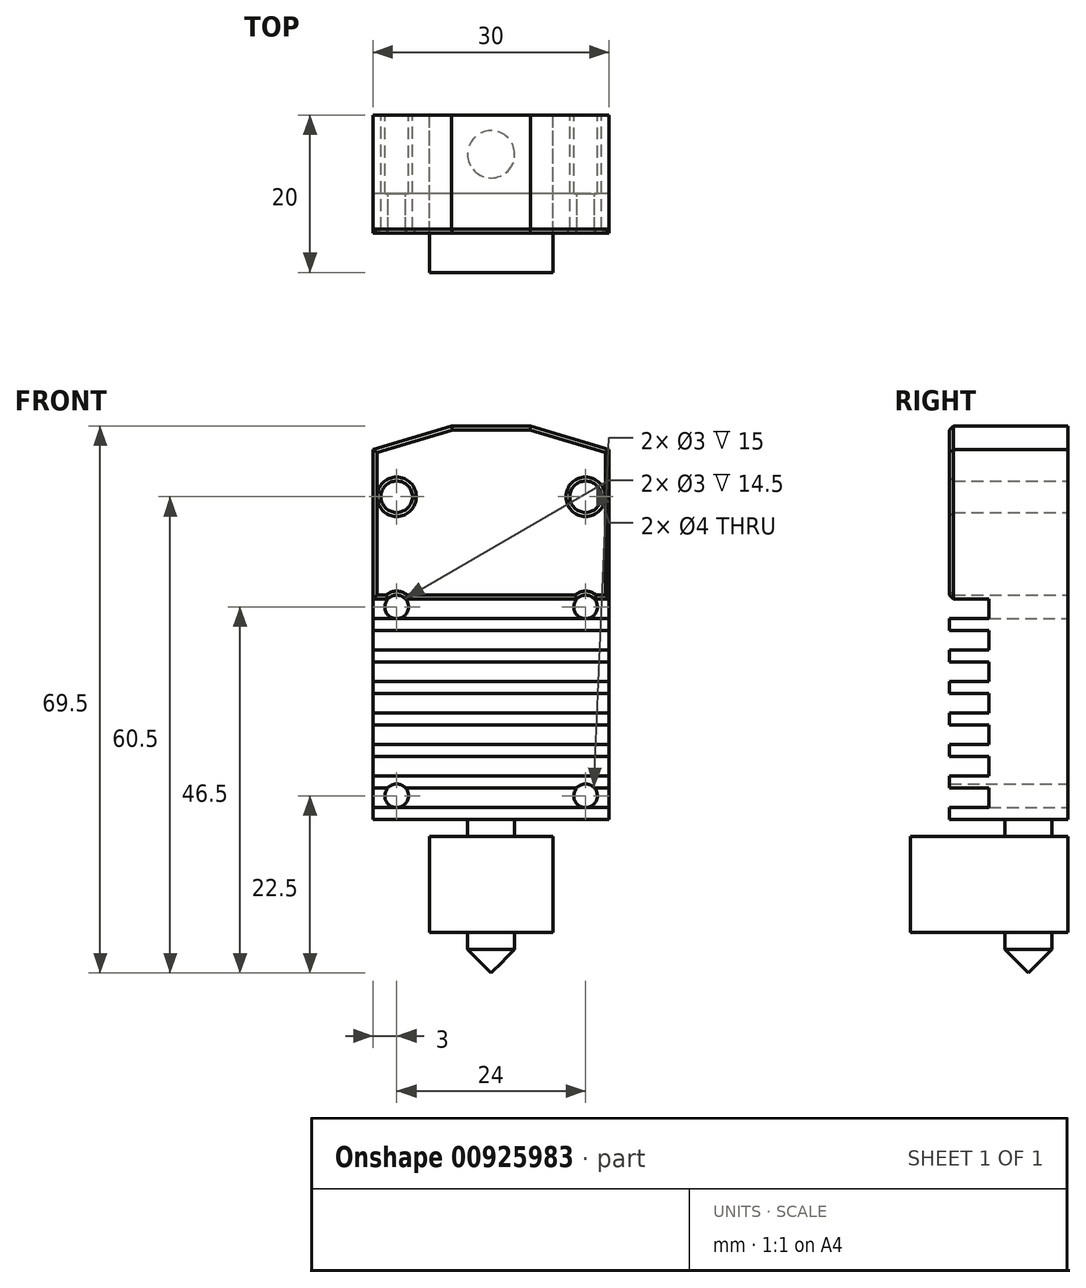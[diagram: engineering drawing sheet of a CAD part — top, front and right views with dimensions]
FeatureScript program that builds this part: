
annotation { "Feature Type Name" : "Feature", "Feature Type Description" : "" }
export const myFeature = defineFeature(function(context is Context, id is Id, definition is map)
    precondition{}
    {
        {
            var Q0;
            Q0=qCreatedBy(makeId("Front.planeOp"),FACE);
            var sketch = newSketch(context, id + "F0", { "sketchPlane" : qUnion([Q0])});
            skLineSegment(sketch, "E0", {"start": v(0, 0) * mm, "end": v(-15, 0) * mm});
            skLineSegment(sketch, "E1", {"start": v(-15, 0) * mm, "end": v(-15, -50) * mm});
            skLineSegment(sketch, "E2", {"start": v(-15, -50) * mm, "end": v(0, -50) * mm});
            skLineSegment(sketch, "E3", {"start": v(0, 0) * mm, "end": v(0, -50) * mm, "construction": true});
            skLineSegment(sketch, "E4.MirrorCS", {"start": v(0, 0) * mm, "end": v(15, 0) * mm});
            skLineSegment(sketch, "E5.MirrorCS", {"start": v(15, 0) * mm, "end": v(15, -50) * mm});
            skLineSegment(sketch, "E6.MirrorCS", {"start": v(15, -50) * mm, "end": v(0, -50) * mm});
            skCircle(sketch, "E7", {"center": v(-12, -47) * mm, "radius": 1.5 * mm});
            skCircle(sketch, "E8", {"center": v(-12, -23) * mm, "radius": 1.5 * mm});
            skCircle(sketch, "E9", {"center": v(-12, -9) * mm, "radius": 2 * mm});
            skCircle(sketch, "E10.MirrorC", {"center": v(12, -9) * mm, "radius": 2 * mm});
            skCircle(sketch, "E11.MirrorC", {"center": v(12, -23) * mm, "radius": 1.5 * mm});
            skCircle(sketch, "E12.MirrorC", {"center": v(12, -47) * mm, "radius": 1.5 * mm});
            skSolve(sketch);
        }
        {
            var Q0;
            Q0=makeQuery(id+"F0.imprint","IMPRINT",FACE,{"disambiguationData":[TD([[makeQuery(id+"F0.imprint","IMPRINT",EDGE,{"derivedFrom":sQuery(id+"F0.wireOp",EDGE,"E0")}),1.0]])]});
            extrude(context, id + "F1", {"entities" : qUnion([Q0]), "depth" : 15 * mm, "offsetDistance" : 25 * mm});
        }
        {
            var Q0;
            Q0=makeQuery(id+"F1.opExtrude","SWEPT_FACE",FACE,{"disambiguationData":[OSD([sQuery(id+"F0.wireOp",EDGE,"E1")])]});
            var sketch = newSketch(context, id + "F2", { "sketchPlane" : qUnion([Q0])});
            skLineSegment(sketch, "E13.bottom", {"start": v(15, -48.5) * mm, "end": v(10, -48.5) * mm});
            skLineSegment(sketch, "E13.top", {"start": v(15, -46) * mm, "end": v(10, -46) * mm});
            skLineSegment(sketch, "E13.left", {"start": v(15, -48.5) * mm, "end": v(15, -46) * mm});
            skLineSegment(sketch, "E13.right", {"start": v(10, -48.5) * mm, "end": v(10, -46) * mm});
            skLineSegment(sketch, "E14.0.1.0", {"start": v(15, -42) * mm, "end": v(10, -42) * mm});
            skLineSegment(sketch, "E14.0.1.1", {"start": v(15, -44.5) * mm, "end": v(10, -44.5) * mm});
            skLineSegment(sketch, "E14.0.1.2", {"start": v(10, -44.5) * mm, "end": v(10, -42) * mm});
            skLineSegment(sketch, "E14.0.1.3", {"start": v(15, -44.5) * mm, "end": v(15, -42) * mm});
            skLineSegment(sketch, "E14.0.2.0", {"start": v(15, -38) * mm, "end": v(10, -38) * mm});
            skLineSegment(sketch, "E14.0.2.1", {"start": v(15, -40.5) * mm, "end": v(10, -40.5) * mm});
            skLineSegment(sketch, "E14.0.2.2", {"start": v(10, -40.5) * mm, "end": v(10, -38) * mm});
            skLineSegment(sketch, "E14.0.2.3", {"start": v(15, -40.5) * mm, "end": v(15, -38) * mm});
            skLineSegment(sketch, "E14.0.3.0", {"start": v(15, -34) * mm, "end": v(10, -34) * mm});
            skLineSegment(sketch, "E14.0.3.1", {"start": v(15, -36.5) * mm, "end": v(10, -36.5) * mm});
            skLineSegment(sketch, "E14.0.3.2", {"start": v(10, -36.5) * mm, "end": v(10, -34) * mm});
            skLineSegment(sketch, "E14.0.3.3", {"start": v(15, -36.5) * mm, "end": v(15, -34) * mm});
            skLineSegment(sketch, "E14.0.4.0", {"start": v(15, -30) * mm, "end": v(10, -30) * mm});
            skLineSegment(sketch, "E14.0.4.1", {"start": v(15, -32.5) * mm, "end": v(10, -32.5) * mm});
            skLineSegment(sketch, "E14.0.4.2", {"start": v(10, -32.5) * mm, "end": v(10, -30) * mm});
            skLineSegment(sketch, "E14.0.4.3", {"start": v(15, -32.5) * mm, "end": v(15, -30) * mm});
            skLineSegment(sketch, "E14.0.5.0", {"start": v(15, -26) * mm, "end": v(10, -26) * mm});
            skLineSegment(sketch, "E14.0.5.1", {"start": v(15, -28.5) * mm, "end": v(10, -28.5) * mm});
            skLineSegment(sketch, "E14.0.5.2", {"start": v(10, -28.5) * mm, "end": v(10, -26) * mm});
            skLineSegment(sketch, "E14.0.5.3", {"start": v(15, -28.5) * mm, "end": v(15, -26) * mm});
            skLineSegment(sketch, "E14.0.6.0", {"start": v(15, -22) * mm, "end": v(10, -22) * mm});
            skLineSegment(sketch, "E14.0.6.1", {"start": v(15, -24.5) * mm, "end": v(10, -24.5) * mm});
            skLineSegment(sketch, "E14.0.6.2", {"start": v(10, -24.5) * mm, "end": v(10, -22) * mm});
            skLineSegment(sketch, "E14.0.6.3", {"start": v(15, -24.5) * mm, "end": v(15, -22) * mm});
            skLineSegment(sketch, "E14.direction1", {"start": v(10, -46) * mm, "end": v(40, -46) * mm, "construction": true});
            skLineSegment(sketch, "E14.direction2", {"start": v(10, -46) * mm, "end": v(10, -42) * mm, "construction": true});
            skSolve(sketch);
        }
        {
            var Q0;
            Q0 = qSketchRegion(id + "F2", true);
            extrude(context, id + "F3", {"entities" : qUnion([Q0]), "operationType" : NewBodyOperationType.REMOVE, "endBound" : BoundingType.THROUGH_ALL, "oppositeDirection" : true, "depth" : 25 * mm, "offsetDistance" : 25 * mm});
        }
        {
            var Q0;
            Q0=makeQuery(id+"F1.opExtrude","SWEPT_FACE",FACE,{"disambiguationData":[OSD([sQuery(id+"F0.wireOp",EDGE,"E2"),sQuery(id+"F0.wireOp",EDGE,"E6.MirrorCS")])]});
            var sketch = newSketch(context, id + "F4", { "sketchPlane" : qUnion([Q0])});
            skPoint(sketch, "E15.0", {"position": v(0, 10) * mm});
            skLineSegment(sketch, "E16", {"start": v(0, 0) * mm, "end": v(0, 10) * mm, "construction": true});
            skCircle(sketch, "E17", {"center": v(0, 5) * mm, "radius": 3 * mm});
            skSolve(sketch);
        }
        {
            var Q0;
            Q0=makeQuery(id+"F1.opExtrude","SWEPT_EDGE",EDGE,{"disambiguationData":[OSD([sQuery(id+"F0.wireOp",EDGE,"E0"),sQuery(id+"F0.wireOp",EDGE,"E1")])]});
            var Q1;
            Q1=makeQuery(id+"F1.opExtrude","SWEPT_EDGE",EDGE,{"disambiguationData":[OSD([sQuery(id+"F0.wireOp",EDGE,"E4.MirrorCS"),sQuery(id+"F0.wireOp",EDGE,"E5.MirrorCS")])]});
            chamfer(context, id + "F5", {"entities" : qUnion([Q0, Q1]), "chamferType" : ChamferType.TWO_OFFSETS, "width1" : 3 * mm, "oppositeDirection" : false, "width2" : 10 * mm, "tangentPropagation" : true});
        }
        {
            var Q0;
            {var subQ0=sQuery(id+"F0.wireOp",EDGE,"E5.MirrorCS");var subQ1=sQuery(id+"F0.wireOp",EDGE,"E1");var subQ2=sQuery(id+"F0.wireOp",EDGE,"E8");var subQ3=sQuery(id+"F0.wireOp",EDGE,"E4.MirrorCS");var subQ4=sQuery(id+"F0.wireOp",EDGE,"E0");var subQ5=sQuery(id+"F0.wireOp",EDGE,"E9");var subQ6=sQuery(id+"F0.wireOp",EDGE,"E10.MirrorC");var subQ7=sQuery(id+"F0.wireOp",EDGE,"E11.MirrorC");Q0=makeQuery(id+"F3.boolean.opBoolean","SPLIT",FACE,{"disambiguationData":[TD([makeQuery(id+"F1.opExtrude","SWEPT_FACE",FACE,{"disambiguationData":[OSD([subQ2])]})])],"derivedFrom":makeQuery(id+"F1.opExtrude","CAP_FACE",FACE,{"disambiguationData":[OSD([subQ4,subQ1,sQuery(id+"F0.wireOp",EDGE,"E2"),subQ3,subQ0,sQuery(id+"F0.wireOp",EDGE,"E6.MirrorCS"),sQuery(id+"F0.wireOp",EDGE,"E7"),subQ2,subQ5,subQ6,subQ7,sQuery(id+"F0.wireOp",EDGE,"E12.MirrorC")])],"isStart":false})});}
            chamfer(context, id + "F6", {"entities" : qUnion([Q0]), "width" : 0.5 * mm, "tangentPropagation" : true});
        }
        {
            var Q0;
            Q0=makeQuery(id+"F4.imprint","IMPRINT",FACE,{"disambiguationData":[TD([[makeQuery(id+"F4.imprint","IMPRINT",EDGE,{"derivedFrom":sQuery(id+"F4.wireOp",EDGE,"E17")}),1.0]])]});
            extrude(context, id + "F7", {"entities" : qUnion([Q0]), "operationType" : NewBodyOperationType.ADD, "depth" : 19.5 * mm, "offsetDistance" : 25 * mm});
        }
        {
            var Q0;
            Q0=makeQuery(id+"F7.opExtrude","CAP_EDGE",EDGE,{"disambiguationData":[OSD([sQuery(id+"F4.wireOp",EDGE,"E17")])],"isStart":false});
            chamfer(context, id + "F8", {"entities" : qUnion([Q0]), "width" : 3 * mm, "tangentPropagation" : true});
        }
        {
            var Q0;
            Q0=qCreatedBy(makeId("Front.planeOp"),FACE);
            var sketch = newSketch(context, id + "F9", { "sketchPlane" : qUnion([Q0])});
            skLineSegment(sketch, "E18.bottom", {"start": v(7.83, -64.37) * mm, "end": v(-7.83, -64.37) * mm});
            skLineSegment(sketch, "E18.top", {"start": v(7.83, -52.17) * mm, "end": v(-7.83, -52.17) * mm});
            skLineSegment(sketch, "E18.left", {"start": v(7.83, -64.37) * mm, "end": v(7.83, -52.17) * mm});
            skLineSegment(sketch, "E18.right", {"start": v(-7.83, -64.37) * mm, "end": v(-7.83, -52.17) * mm});
            skPoint(sketch, "E18.middle", {"position": v(0, -58.27) * mm});
            skSolve(sketch);
        }
        {
            var Q0;
            Q0=makeQuery(id+"F9.imprint","IMPRINT",FACE,{"disambiguationData":[TD([[makeQuery(id+"F9.imprint","IMPRINT",EDGE,{"derivedFrom":sQuery(id+"F9.wireOp",EDGE,"E18.bottom")}),-1.0]])]});
            extrude(context, id + "F10", {"entities" : qUnion([Q0]), "operationType" : NewBodyOperationType.ADD, "depth" : 20 * mm, "offsetDistance" : 25 * mm});
        }
    });
